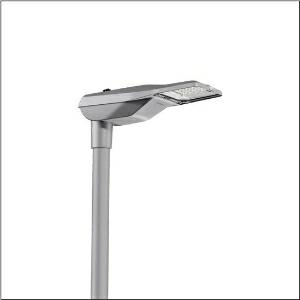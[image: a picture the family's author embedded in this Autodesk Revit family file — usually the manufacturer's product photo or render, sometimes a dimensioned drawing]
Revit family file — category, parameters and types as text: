
# Revit family: streetlight_sl_21_micro___st1_5a_5xe1p43s08db_ce40
name_source: partatom
category: Lighting Fixtures
units: mm (PartAtom-declared; Revit-internal decimal feet)

## family parameters
Cut with Voids When Loaded = No
Host = Face
Light Source = No
Part Type = Normal
Room Calculation Point = No
Round Connector Dimension = Use Diameter
Shared = No

## types (1)
- --- (1 x LED, 5230 lm, 39.1 W, 4000K)
    Apparent Load = 39 VA
    CIE Flux Codes = 22 53 95 100 100
    Color Rendering = 70
    Color Temperature = 4000K
    Default Elevation = 1800 mm
    Description = Streetlight SL 21 micro, mast luminaire, primary light control with lens, of PMMA, primary optical cover: cover, of toughened safety glass, transparent, light distribution: ST1.5a, light emission: direct distribution, primary light characteristic: asymmetric, installation type: side-entry, post-top, LED, High Power LED, rated luminous flux: 5.230lm, luminous efficacy: 134lm/W, light colour: 740, colour temperature: 4000K, control gear: D4i, control: flexible luminous flux parameterisation, time-dependent luminous flux control, constant luminous flux control, overheat protection, pre-setting: logarithmic dimming characteristic, mains connection: 220..240V, AC, 50/60Hz, start of lifetime: 39W, end of service life: 41W, reduction: 18W, luminaire housing, of diecast aluminium, powder-coated, SITECO metallic grey (DB 702S), corrosivity category C5 high according to DIN EN ISO 12944, please order mast flange separately, inclination adjustable: 0°, 5°, 10°, 15°, sealing non-destructively replaceable, multi-level sealing system, length: 528mm, width: 235mm, height: 110mm, mast flange for spigot size: 42mm (side-entry): 5XC10008XM4, 60/48mm (side-entry/post-top): 5XC10108XM2, 76/60mm (side-entry/post-top): 5XC10108XM1, Smart Interface above, protection rating (complete): IP66, insulation class (complete): insulation class II (safety insulation), certification: CE, ENEC, ENEC+, VDE, impact resistance: IK10, permissible operating ambient temperature for outdoor applications: -40..+50°C, standard-compliant lighting for roads and squares, packaging unit: 1 piece

Light Distribution: ST1.5a
    Height = 110 mm
    Lamp = 1 x LED
    Lamp Light Flux = 5230 lm
    Lamp Power = 39.1 W
    Lamp count = 1
    Length = 528 mm
    Luminous efficacy = 134 lm/W
    Manufacturer = Siteco
    ModVariant = No
    Model = 5XE1P43S08DB
    Number of Poles = 1
    OnlyDefault = Yes
    Power Factor = 1
    Product Name = Streetlight SL 21 micro | ST1.5a
    Product group = mast luminaire | pylon top
    ProductGroupID = 6100
    Protection Class = Protection class II
    Protection Degree = IP 66
    RLX_Detail_Level = 1
    RLX_Emergency_Light_Flux = 0 lm
    RLX_Emergency_Type = 0
    RLX_Emergency_Type_DB = No
    RlxData = <blob elided: 101865 chars, md5=2e7398f7>
    Socket = socket
    Standby Power = 0 W
    System Light Flux = 5230 lm
    System Power = 39 W
    Type Comments = factory setting: luminous flux: 100 % | dim-lin: 254 | 765 mA
    Type Image = l_1277292.jpg
    URL = http://relux.com
    VarID = @adj_153203
    Voltage = 0 V
    Weight = 0.00 kg
    Width = 235 mm

## geometry (parser evidence)
native form markers: Blend x4, Sweep x11
no freeform markers — native parametric forms only
